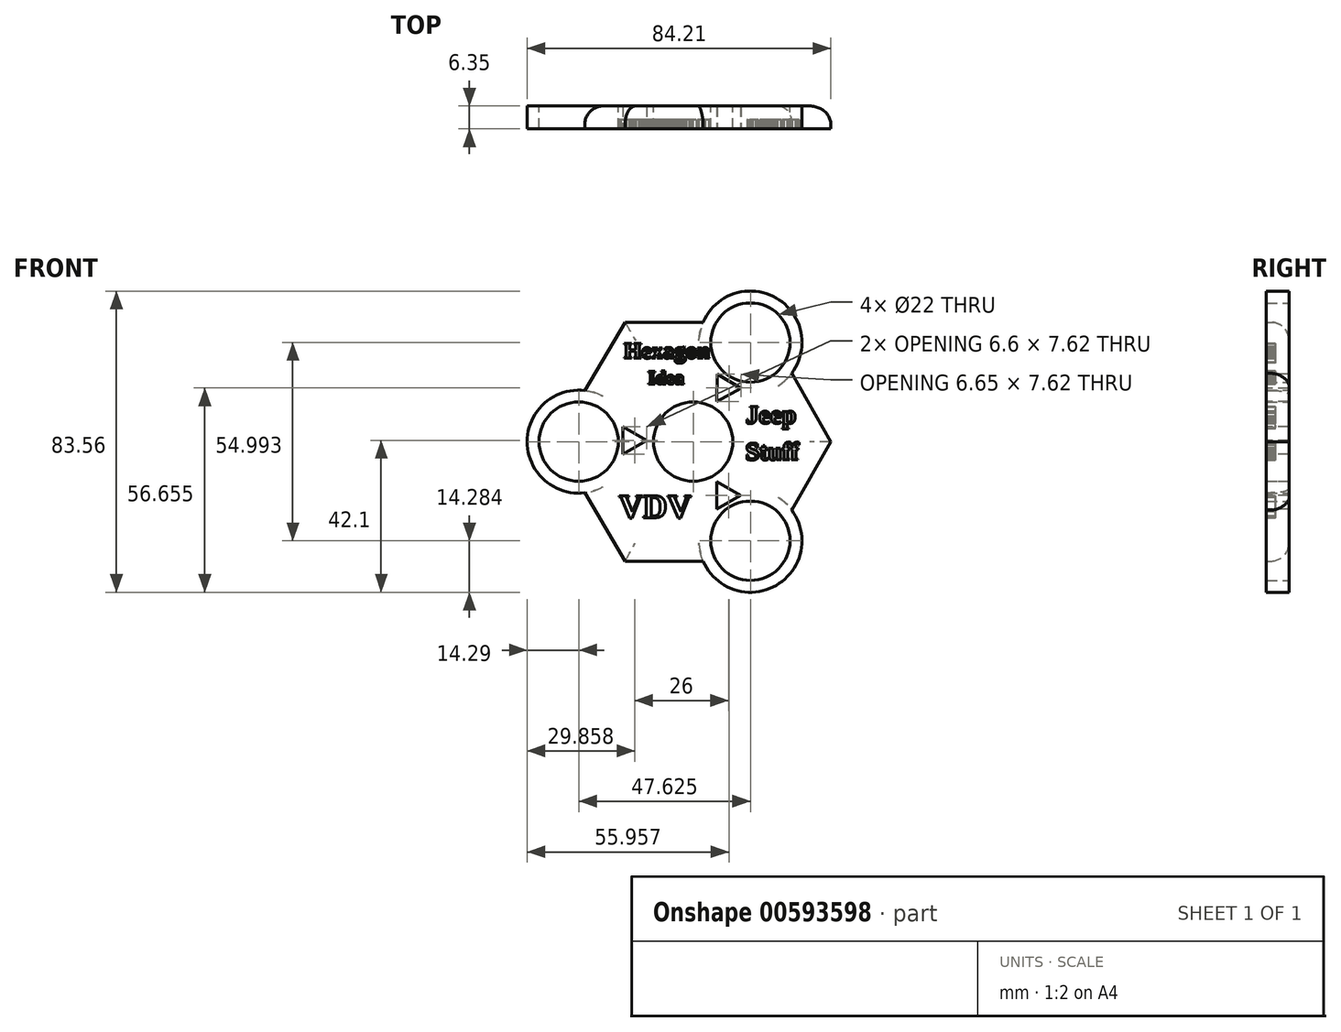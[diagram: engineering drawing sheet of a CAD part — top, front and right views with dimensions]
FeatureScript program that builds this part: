
annotation { "Feature Type Name" : "Feature", "Feature Type Description" : "" }
export const myFeature = defineFeature(function(context is Context, id is Id, definition is map)
    precondition{}
    {
        {
            var Q0;
            Q0=qCreatedBy(makeId("Front.planeOp"),FACE);
            var sketch = newSketch(context, id + "F0", { "sketchPlane" : qUnion([Q0])});
            skCircle(sketch, "E0", {"center": v(0, 0) * mm, "radius": 14.29 * mm});
            skCircle(sketch, "E1", {"center": v(0, 0) * mm, "radius": 11 * mm});
            skCircle(sketch, "E2", {"center": v(-31.75, 0) * mm, "radius": 14.29 * mm});
            skCircle(sketch, "E3", {"center": v(-31.75, 0) * mm, "radius": 11 * mm});
            skCircle(sketch, "E4.1.0", {"center": v(15.87, -27.5) * mm, "radius": 14.29 * mm});
            skCircle(sketch, "E4.1.1", {"center": v(15.87, -27.5) * mm, "radius": 11 * mm});
            skCircle(sketch, "E4.2.0", {"center": v(15.88, 27.5) * mm, "radius": 14.29 * mm});
            skCircle(sketch, "E4.2.1", {"center": v(15.88, 27.5) * mm, "radius": 11 * mm});
            skSolve(sketch);
        }
        {
            var Q0;
            Q0=qCreatedBy(makeId("Front.planeOp"),FACE);
            var sketch = newSketch(context, id + "F1", { "sketchPlane" : qUnion([Q0])});
            skCircle(sketch, "E5.0", {"center": v(15.88, 27.5) * mm, "radius": 11 * mm});
            skCircle(sketch, "E6.0", {"center": v(15.88, 27.5) * mm, "radius": 14.29 * mm});
            skCircle(sketch, "E7.0", {"center": v(0, 0) * mm, "radius": 14.29 * mm});
            skCircle(sketch, "E8.0", {"center": v(0, 0) * mm, "radius": 11 * mm});
            skCircle(sketch, "E9.0", {"center": v(-31.75, 0) * mm, "radius": 14.29 * mm});
            skCircle(sketch, "E10.0", {"center": v(-31.75, 0) * mm, "radius": 11 * mm});
            skArc(sketch, "E11", {"start": v(-30.09, 14.2) * mm, "mid": v(-10.52, 18.23) * mm, "end": v(2.76, 33.15) * mm});
            skArc(sketch, "E12", {"start": v(27.33, 18.96) * mm, "mid": v(21.05, 0) * mm, "end": v(27.33, -18.96) * mm});
            skArc(sketch, "E13", {"start": v(2.76, -33.15) * mm, "mid": v(-10.52, -18.23) * mm, "end": v(-30.09, -14.2) * mm});
            skCircle(sketch, "E14.0", {"center": v(15.87, -27.5) * mm, "radius": 14.29 * mm});
            skCircle(sketch, "E15.0.0", {"center": v(15.87, -27.5) * mm, "radius": 11 * mm});
            skLineSegment(sketch, "E16", {"start": v(2.76, 33.15) * mm, "end": v(-18.9, 33.15) * mm});
            skLineSegment(sketch, "E17", {"start": v(-18.9, 33.15) * mm, "end": v(-30.09, 14.2) * mm});
            skLineSegment(sketch, "E18", {"start": v(27.33, 18.96) * mm, "end": v(38.17, 0) * mm});
            skLineSegment(sketch, "E19", {"start": v(38.17, 0) * mm, "end": v(27.33, -18.96) * mm});
            skLineSegment(sketch, "E20", {"start": v(2.76, -33.15) * mm, "end": v(-18.92, -33.15) * mm});
            skLineSegment(sketch, "E21", {"start": v(-18.92, -33.15) * mm, "end": v(-30.09, -14.2) * mm});
            skSolve(sketch);
        }
        {
            var Q0;
            Q0 = qSketchRegion(id + "F1", true);
            extrude(context, id + "F2", {"entities" : qUnion([Q0]), "depth" : 6.35 * mm, "offsetDistance" : 25.4 * mm});
        }
        {
            var Q0;
            Q0=makeQuery(id+"F0.imprint","IMPRINT",FACE,{"disambiguationData":[TD([[makeQuery(id+"F0.imprint","IMPRINT",EDGE,{"derivedFrom":sQuery(id+"F0.wireOp",EDGE,"E0")}),1.0]])]});
            extrude(context, id + "F3", {"entities" : qUnion([Q0]), "operationType" : NewBodyOperationType.ADD, "depth" : 6.35 * mm, "offsetDistance" : 25.4 * mm});
        }
        {
            var Q0;
            Q0=makeQuery(id+"F2.opExtrude","CAP_EDGE",EDGE,{"disambiguationData":[OSD([sQuery(id+"F1.wireOp",EDGE,"E16")])],"isStart":true});
            var Q1;
            Q1=makeQuery(id+"F2.opExtrude","CAP_EDGE",EDGE,{"disambiguationData":[OSD([sQuery(id+"F1.wireOp",EDGE,"E17")])],"isStart":true});
            var Q2;
            Q2=makeQuery(id+"F2.opExtrude","CAP_EDGE",EDGE,{"disambiguationData":[OSD([sQuery(id+"F1.wireOp",EDGE,"E21")])],"isStart":true});
            var Q3;
            Q3=makeQuery(id+"F2.opExtrude","CAP_EDGE",EDGE,{"disambiguationData":[OSD([sQuery(id+"F1.wireOp",EDGE,"E20")])],"isStart":true});
            var Q4;
            Q4=makeQuery(id+"F2.opExtrude","CAP_EDGE",EDGE,{"disambiguationData":[OSD([sQuery(id+"F1.wireOp",EDGE,"E19")])],"isStart":true});
            var Q5;
            Q5=makeQuery(id+"F2.opExtrude","CAP_EDGE",EDGE,{"disambiguationData":[OSD([sQuery(id+"F1.wireOp",EDGE,"E18")])],"isStart":true});
            fillet(context, id + "F4", {"entities" : qUnion([Q0, Q1, Q2, Q3, Q4, Q5]), "radius" : 5.08 * mm, "tangentPropagation" : true, "allowEdgeOverflow" : false});
        }
        {
            var Q0;
            Q0=makeQuery(id+"F3.boolean.opBoolean","MERGE",FACE,{"derivedFrom":[makeQuery(id+"F2.opExtrude","CAP_FACE",FACE,{"disambiguationData":[OSD([sQuery(id+"F1.wireOp",EDGE,"E5.0"),sQuery(id+"F1.wireOp",EDGE,"E6.0"),sQuery(id+"F1.wireOp",EDGE,"E7.0"),sQuery(id+"F1.wireOp",EDGE,"E9.0"),sQuery(id+"F1.wireOp",EDGE,"E10.0"),sQuery(id+"F1.wireOp",EDGE,"E14.0"),sQuery(id+"F1.wireOp",EDGE,"E15.0.0"),sQuery(id+"F1.wireOp",EDGE,"E16"),sQuery(id+"F1.wireOp",EDGE,"E17"),sQuery(id+"F1.wireOp",EDGE,"E18"),sQuery(id+"F1.wireOp",EDGE,"E19"),sQuery(id+"F1.wireOp",EDGE,"E20"),sQuery(id+"F1.wireOp",EDGE,"E21")])],"isStart":false}),makeQuery(id+"F3.opExtrude","CAP_FACE",FACE,{"disambiguationData":[OSD([sQuery(id+"F0.wireOp",EDGE,"E0"),sQuery(id+"F0.wireOp",EDGE,"E1")])],"isStart":false})]});
            var sketch = newSketch(context, id + "F5", { "sketchPlane" : qUnion([Q0])});
            skPoint(sketch, "E22.secondSnap0", {"position": v(32.75, -9.48) * mm});
            skPoint(sketch, "E23", {"position": v(-24.5, 23.67) * mm});
            skText(sketch, "E24", { "text": "Hexagon", "fontName": "Tinos-Bold.ttf"});
            skText(sketch, "E25", { "text": "Idea", "fontName": "Tinos-Bold.ttf"});
            skText(sketch, "E26", { "text": "VDV", "fontName": "Tinos-Bold.ttf"});
            skText(sketch, "E27", { "text": "Jeep", "fontName": "Tinos-Bold.ttf"});
            skText(sketch, "E28", { "text": "Stuff", "fontName": "Tinos-Bold.ttf"});
            const initialGuessF5  = {"E24": [-0.01923, 0.02315, 1, 0, 0.00454], "E25": [-0.01251, 0.01599, 1, 0, 0.0038], "E26": [-0.02066, -0.02108, 1, 0, 0.0067], "E27": [0.0146, 0.00508, 1, 0, 0.00517], "E28": [0.0145, -0.00506, 1, 0, 0.00506]};
            skSetInitialGuess(sketch, initialGuessF5);
            skSolve(sketch);
        }
        {
            var Q0;
            Q0 = qSketchRegion(id + "F5", true);
            extrude(context, id + "F6", {"entities" : qUnion([Q0]), "operationType" : NewBodyOperationType.REMOVE, "oppositeDirection" : true, "depth" : 2.54 * mm, "offsetDistance" : 25.4 * mm});
        }
        {
            var Q0;
            {var subQ0=sQuery(id+"F0.wireOp",EDGE,"E1");var subQ1=sQuery(id+"F1.wireOp",EDGE,"E21");var subQ2=sQuery(id+"F1.wireOp",EDGE,"E20");var subQ3=sQuery(id+"F1.wireOp",EDGE,"E10.0");var subQ4=sQuery(id+"F1.wireOp",EDGE,"E6.0");var subQ5=sQuery(id+"F1.wireOp",EDGE,"E9.0");var subQ6=sQuery(id+"F1.wireOp",EDGE,"E5.0");var subQ7=sQuery(id+"F1.wireOp",EDGE,"E19");var subQ8=sQuery(id+"F1.wireOp",EDGE,"E18");var subQ9=sQuery(id+"F1.wireOp",EDGE,"E14.0");var subQ10=sQuery(id+"F1.wireOp",EDGE,"E15.0.0");var subQ11=sQuery(id+"F1.wireOp",EDGE,"E17");var subQ12=sQuery(id+"F1.wireOp",EDGE,"E16");Q0=makeQuery(id+"F6.boolean.opBoolean","SPLIT",FACE,{"disambiguationData":[TD([makeQuery(id+"F2.opExtrude","SWEPT_FACE",FACE,{"disambiguationData":[OSD([subQ6])]})])],"derivedFrom":makeQuery(id+"F3.boolean.opBoolean","MERGE",FACE,{"derivedFrom":[makeQuery(id+"F2.opExtrude","CAP_FACE",FACE,{"disambiguationData":[OSD([subQ6,subQ4,sQuery(id+"F1.wireOp",EDGE,"E7.0"),subQ5,subQ3,subQ9,subQ10,subQ12,subQ11,subQ8,subQ7,subQ2,subQ1])],"isStart":false}),makeQuery(id+"F3.opExtrude","CAP_FACE",FACE,{"disambiguationData":[OSD([sQuery(id+"F0.wireOp",EDGE,"E0"),subQ0])],"isStart":false})]})});}
            var sketch = newSketch(context, id + "F7", { "sketchPlane" : qUnion([Q0])});
            skLineSegment(sketch, "E29", {"start": v(6.7, 18.68) * mm, "end": v(13.24, 14.78) * mm});
            skLineSegment(sketch, "E30", {"start": v(13.24, 14.78) * mm, "end": v(6.6, 11.07) * mm});
            skLineSegment(sketch, "E31", {"start": v(6.6, 11.07) * mm, "end": v(6.7, 18.68) * mm});
            skLineSegment(sketch, "E32", {"start": v(-19.48, -3.49) * mm, "end": v(-19.48, 4.13) * mm});
            skLineSegment(sketch, "E33", {"start": v(-19.48, 4.13) * mm, "end": v(-12.88, 0.32) * mm});
            skLineSegment(sketch, "E34", {"start": v(-12.88, 0.32) * mm, "end": v(-19.48, -3.49) * mm});
            skLineSegment(sketch, "E35", {"start": v(13.12, -14.92) * mm, "end": v(6.52, -18.73) * mm});
            skLineSegment(sketch, "E36", {"start": v(6.52, -18.73) * mm, "end": v(6.52, -11.11) * mm});
            skLineSegment(sketch, "E37", {"start": v(6.52, -11.11) * mm, "end": v(13.12, -14.92) * mm});
            skSolve(sketch);
        }
        {
            var Q0;
            Q0 = qSketchRegion(id + "F7", true);
            extrude(context, id + "F8", {"entities" : qUnion([Q0]), "operationType" : NewBodyOperationType.REMOVE, "oppositeDirection" : true, "depth" : 25.4 * mm, "offsetDistance" : 25.4 * mm});
        }
    });
